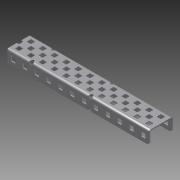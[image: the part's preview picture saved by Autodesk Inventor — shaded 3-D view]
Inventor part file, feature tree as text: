
AUTODESK INVENTOR PART (.ipt)
format: ipt  version: 2012 (Build 160160000, 160)  size: 854,528 bytes
history: native  units: in
note: dims shown in document units (in); Inventor stores cm internally (conversion verified against a paired STEP export)
features: other x1, imported_body x1, plane x1, split x1
ambient origin geometry x8: Origin, YZ Plane, XZ Plane, XY Plane, X Axis, Y Axis, Z Axis, Center Point
feature tree (4):
  parser-record x1  (decoder bookkeeping rows leaked as tree rows — omitted from the tree; the rows remain in map.json)
  imported_body  "Base1"
  plane  "Work Plane1"
  split  "Split1"
